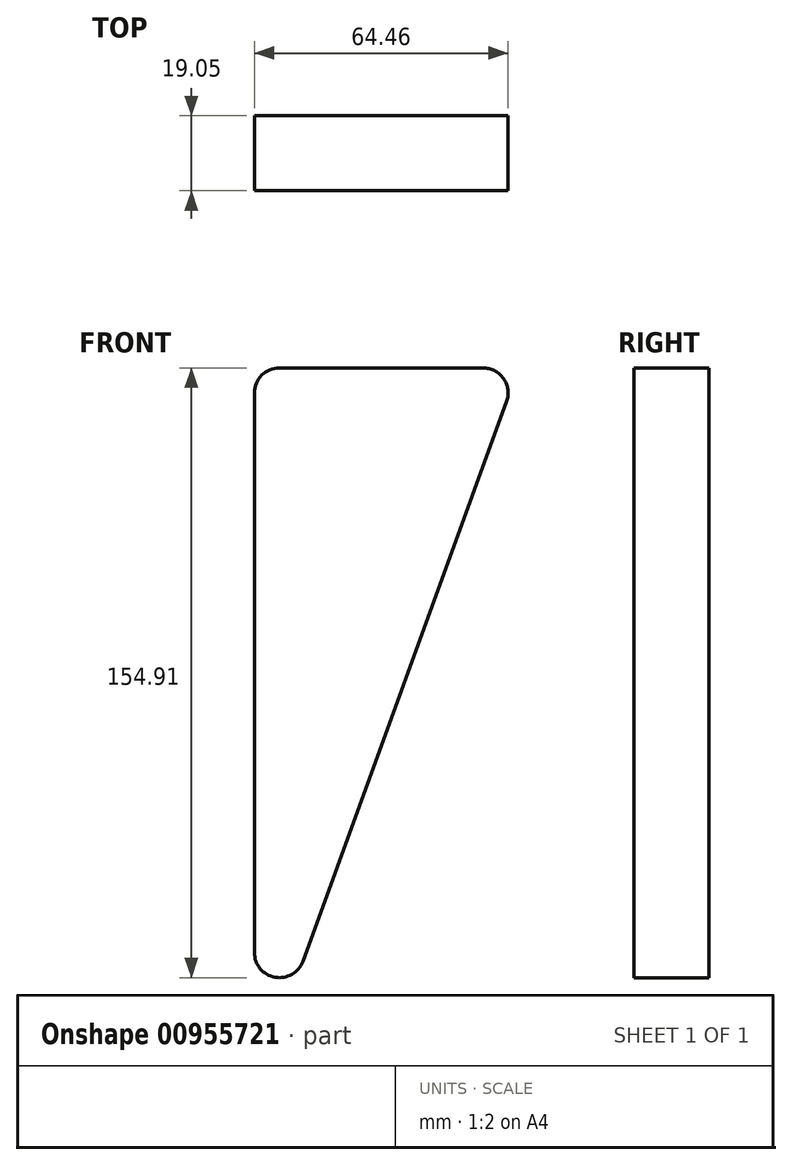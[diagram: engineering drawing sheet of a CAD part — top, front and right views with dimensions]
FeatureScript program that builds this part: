
annotation { "Feature Type Name" : "Feature", "Feature Type Description" : "" }
export const myFeature = defineFeature(function(context is Context, id is Id, definition is map)
    precondition{}
    {
        {
            var Q0;
            Q0=qCreatedBy(makeId("Front.planeOp"),FACE);
            var sketch = newSketch(context, id + "F0", { "sketchPlane" : qUnion([Q0])});
            skLineSegment(sketch, "E0", {"start": v(0, 0) * mm, "end": v(0, 518.57) * mm, "construction": true});
            skLineSegment(sketch, "E1", {"start": v(-127, 0) * mm, "end": v(-177.8, 0) * mm});
            skLineSegment(sketch, "E2", {"start": v(0, 330.2) * mm, "end": v(-9.53, 330.2) * mm});
            skLineSegment(sketch, "E3", {"start": v(-9.53, 330.2) * mm, "end": v(-9.53, 482.6) * mm});
            skLineSegment(sketch, "E4", {"start": v(-9.53, 482.6) * mm, "end": v(-114.43, 482.6) * mm});
            skLineSegment(sketch, "E5", {"start": v(-114.43, 482.6) * mm, "end": v(-114.43, 508) * mm});
            skLineSegment(sketch, "E6", {"start": v(-114.43, 508) * mm, "end": v(-152.53, 508) * mm});
            skLineSegment(sketch, "E7", {"start": v(-152.53, 508) * mm, "end": v(-152.53, 482.6) * mm});
            skLineSegment(sketch, "E8", {"start": v(-152.53, 482.6) * mm, "end": v(-76.2, 272.9) * mm});
            skFitSpline(sketch, "E9", {"points": [v(-177.8, 0) * mm, v(-76.2, 272.9) * mm], "startDerivative": vector(-14.26, 190.8) * mm, "endDerivative": vector(298.2, 231.03) * mm});
            skFitSpline(sketch, "E10", {"points": [v(-127, 0) * mm, v(0, 177.8) * mm], "startDerivative": vector(15.82, 238.53) * mm, "endDerivative": vector(279.75, 55.19) * mm});
            skLineSegment(sketch, "E11.MirrorCS", {"start": v(114.43, 508) * mm, "end": v(152.53, 508) * mm});
            skLineSegment(sketch, "E12.MirrorCS", {"start": v(152.53, 508) * mm, "end": v(152.53, 482.6) * mm});
            skLineSegment(sketch, "E13.MirrorCS", {"start": v(114.43, 482.6) * mm, "end": v(114.43, 508) * mm});
            skLineSegment(sketch, "E14.MirrorCS", {"start": v(127, 0) * mm, "end": v(177.8, 0) * mm});
            skFitSpline(sketch, "E15.MirrorCS", {"points": [v(177.8, 0) * mm, v(76.2, 272.9) * mm], "startDerivative": vector(14.26, 190.8) * mm, "endDerivative": vector(-298.2, 231.03) * mm});
            skLineSegment(sketch, "E16.MirrorCS", {"start": v(152.53, 482.6) * mm, "end": v(76.2, 272.9) * mm});
            skFitSpline(sketch, "E17.MirrorCS", {"points": [v(127, 0) * mm, v(0, 177.8) * mm], "startDerivative": vector(-15.82, 238.53) * mm, "endDerivative": vector(-279.75, 55.19) * mm});
            skLineSegment(sketch, "E18.MirrorCS", {"start": v(9.53, 482.6) * mm, "end": v(114.43, 482.6) * mm});
            skLineSegment(sketch, "E19.MirrorCS", {"start": v(9.53, 330.2) * mm, "end": v(9.53, 482.6) * mm});
            skLineSegment(sketch, "E20.MirrorCS", {"start": v(0, 330.2) * mm, "end": v(9.53, 330.2) * mm});
            skSolve(sketch);
        }
        {
            var Q0;
            Q0=makeQuery(id+"F0.imprint","IMPRINT",FACE,{"disambiguationData":[TD([[makeQuery(id+"F0.imprint","IMPRINT",EDGE,{"derivedFrom":sQuery(id+"F0.wireOp",EDGE,"E1")}),-1.0]])]});
            extrude(context, id + "F1", {"entities" : qUnion([Q0]), "depth" : 19.05 * mm, "offsetDistance" : 25.4 * mm});
        }
        {
            var Q0;
            Q0=makeQuery(id+"F1.opExtrude","CAP_FACE",FACE,{"disambiguationData":[OSD([sQuery(id+"F0.wireOp",EDGE,"E1"),sQuery(id+"F0.wireOp",EDGE,"E2"),sQuery(id+"F0.wireOp",EDGE,"E3"),sQuery(id+"F0.wireOp",EDGE,"E4"),sQuery(id+"F0.wireOp",EDGE,"E5"),sQuery(id+"F0.wireOp",EDGE,"E6"),sQuery(id+"F0.wireOp",EDGE,"E7"),sQuery(id+"F0.wireOp",EDGE,"E8"),sQuery(id+"F0.wireOp",EDGE,"E9"),sQuery(id+"F0.wireOp",EDGE,"E10"),sQuery(id+"F0.wireOp",EDGE,"E12.MirrorCS"),sQuery(id+"F0.wireOp",EDGE,"E14.MirrorCS"),sQuery(id+"F0.wireOp",EDGE,"E15.MirrorCS"),sQuery(id+"F0.wireOp",EDGE,"E16.MirrorCS"),sQuery(id+"F0.wireOp",EDGE,"E17.MirrorCS"),sQuery(id+"F0.wireOp",EDGE,"E18.MirrorCS"),sQuery(id+"F0.wireOp",EDGE,"E13.MirrorCS"),sQuery(id+"F0.wireOp",EDGE,"E11.MirrorCS"),sQuery(id+"F0.wireOp",EDGE,"E19.MirrorCS"),sQuery(id+"F0.wireOp",EDGE,"E20.MirrorCS")])],"isStart":false});
            var sketch = newSketch(context, id + "F2", { "sketchPlane" : qUnion([Q0])});
            skLineSegment(sketch, "E21.0", {"start": v(-104.08, 442.33) * mm, "end": v(-52.32, 300.12) * mm});
            skLineSegment(sketch, "E22.0", {"start": v(-46.36, 450.85) * mm, "end": v(-98.11, 450.85) * mm});
            skLineSegment(sketch, "E23.0", {"start": v(-40, 302.3) * mm, "end": v(-40, 444.5) * mm});
            skPoint(sketch, "E24.visualSharp", {"position": v(-40, 450.85) * mm});
            skArc(sketch, "E24.filletArc", {"start": v(-40, 444.5) * mm, "mid": v(-41.86, 449) * mm, "end": v(-46.36, 450.85) * mm});
            skPoint(sketch, "E25.visualSharp", {"position": v(-107.18, 450.85) * mm});
            skArc(sketch, "E25.filletArc", {"start": v(-98.11, 450.85) * mm, "mid": v(-103.32, 448.14) * mm, "end": v(-104.08, 442.33) * mm});
            skPoint(sketch, "E26.visualSharp", {"position": v(-40, 266.28) * mm});
            skArc(sketch, "E26.filletArc", {"start": v(-52.32, 300.12) * mm, "mid": v(-45.25, 296.04) * mm, "end": v(-40, 302.3) * mm});
            skArc(sketch, "E27.MirrorCS", {"start": v(40, 444.5) * mm, "mid": v(41.86, 449) * mm, "end": v(46.36, 450.85) * mm});
            skArc(sketch, "E28.MirrorCS", {"start": v(98.11, 450.85) * mm, "mid": v(103.32, 448.14) * mm, "end": v(104.08, 442.33) * mm});
            skArc(sketch, "E29.MirrorCS", {"start": v(52.32, 300.12) * mm, "mid": v(45.25, 296.04) * mm, "end": v(40, 302.3) * mm});
            skPoint(sketch, "E30.MirrorP", {"position": v(40, 450.85) * mm});
            skPoint(sketch, "E31.MirrorP", {"position": v(107.18, 450.85) * mm});
            skPoint(sketch, "E32.MirrorP", {"position": v(40, 266.28) * mm});
            skLineSegment(sketch, "E33.MirrorCS", {"start": v(104.08, 442.33) * mm, "end": v(52.32, 300.12) * mm});
            skLineSegment(sketch, "E34.MirrorCS", {"start": v(40, 302.3) * mm, "end": v(40, 444.5) * mm});
            skLineSegment(sketch, "E35.MirrorCS", {"start": v(46.36, 450.85) * mm, "end": v(98.11, 450.85) * mm});
            skSolve(sketch);
        }
        {
            var Q0;
            Q0=makeQuery(id+"F2.imprint","IMPRINT",FACE,{"disambiguationData":[TD([[makeQuery(id+"F2.imprint","IMPRINT",EDGE,{"derivedFrom":sQuery(id+"F2.wireOp",EDGE,"E21.0")}),1.0]])]});
            var Q1;
            Q1=makeQuery(id+"F2.imprint","IMPRINT",FACE,{"disambiguationData":[TD([[makeQuery(id+"F2.imprint","IMPRINT",EDGE,{"derivedFrom":sQuery(id+"F2.wireOp",EDGE,"E27.MirrorCS")}),-1.0]])]});
            extrude(context, id + "F3", {"entities" : qUnion([Q0, Q1]), "operationType" : NewBodyOperationType.REMOVE, "oppositeDirection" : true, "depth" : 25.4 * mm, "offsetDistance" : 25.4 * mm});
        }
    });
